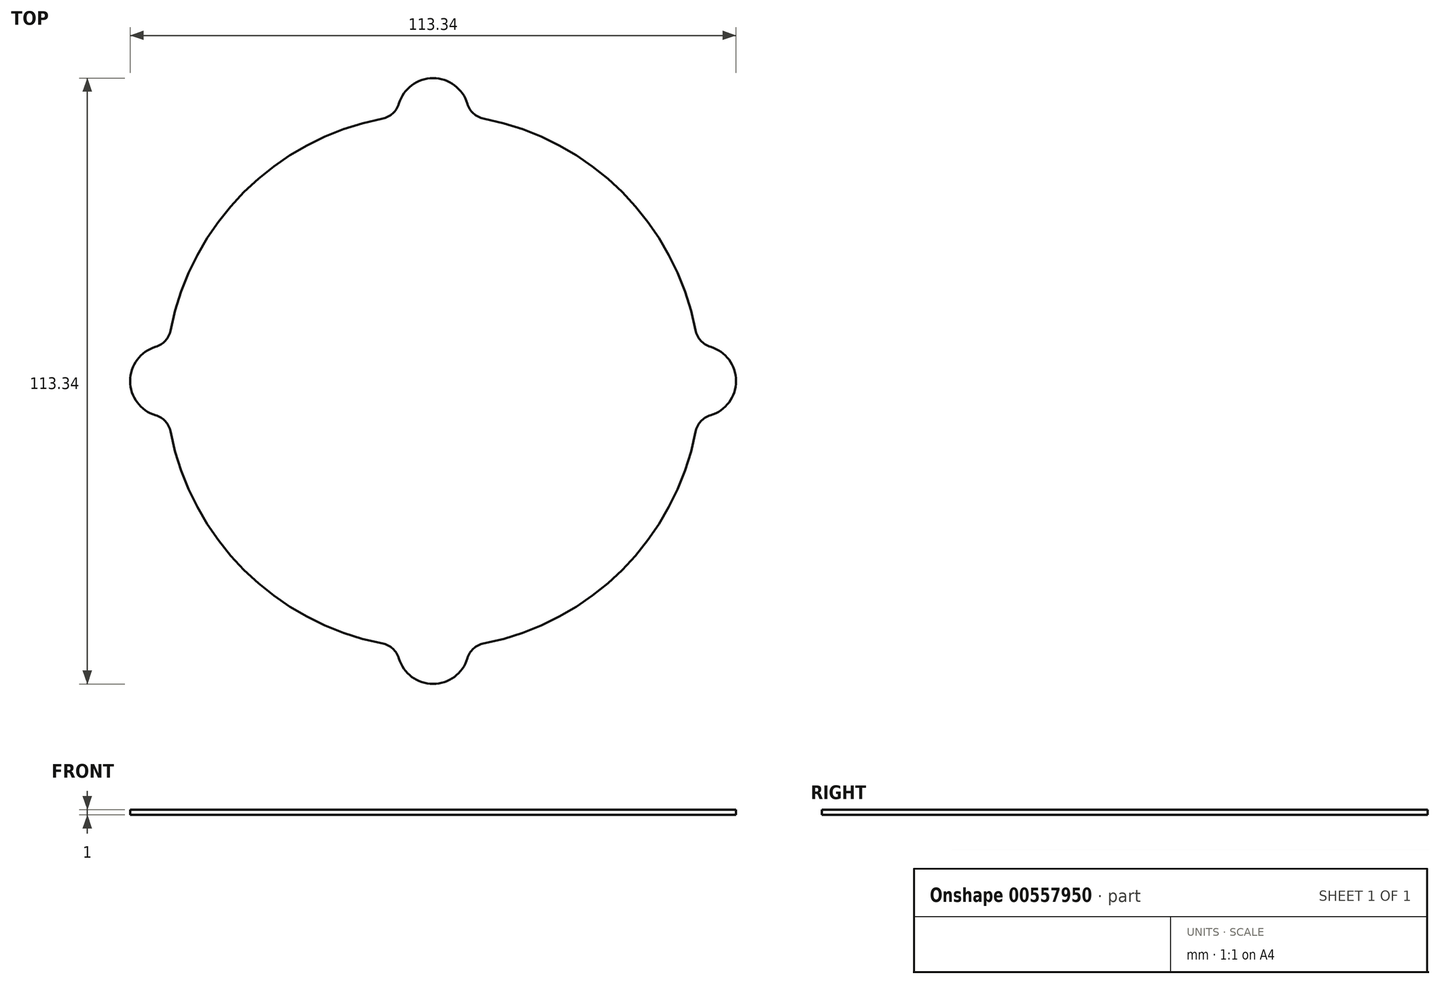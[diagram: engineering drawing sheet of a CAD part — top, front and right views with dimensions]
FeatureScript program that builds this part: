
annotation { "Feature Type Name" : "Feature", "Feature Type Description" : "" }
export const myFeature = defineFeature(function(context is Context, id is Id, definition is map)
    precondition{}
    {
        {
            assignVariable(context, id + "F0", {"name" : "t", "anyValue" : 1});
        }
        {
            var Q0;
            Q0=qCreatedBy(makeId("Top.planeOp"),FACE);
            var sketch = newSketch(context, id + "F1", { "sketchPlane" : qUnion([Q0])});
            skArc(sketch, "E0", {"start": v(-49.1, -9.47) * mm, "mid": v(-35.36, -35.36) * mm, "end": v(-9.47, -49.1) * mm});
            skCircle(sketch, "E1", {"center": v(50, 0) * mm, "radius": 6.67 * mm, "construction": true});
            skArc(sketch, "E2", {"start": v(6.65, 49.56) * mm, "mid": v(0, 56.67) * mm, "end": v(-6.65, 49.56) * mm, "construction": true});
            skArc(sketch, "E3", {"start": v(-49.56, 6.65) * mm, "mid": v(-56.67, 0) * mm, "end": v(-49.56, -6.65) * mm, "construction": true});
            skCircle(sketch, "E4", {"center": v(0, -50) * mm, "radius": 6.67 * mm, "construction": true});
            skArc(sketch, "E5.trimOffspring", {"start": v(-9.47, 49.1) * mm, "mid": v(-35.36, 35.36) * mm, "end": v(-49.1, 9.47) * mm});
            skArc(sketch, "E6", {"start": v(-6.4, -51.89) * mm, "mid": v(0, -56.67) * mm, "end": v(6.4, -51.89) * mm});
            skArc(sketch, "E7.trimOffspring", {"start": v(9.47, -49.1) * mm, "mid": v(35.36, -35.36) * mm, "end": v(49.1, -9.47) * mm});
            skPoint(sketch, "E8.visualSharp", {"position": v(6.65, -49.56) * mm});
            skArc(sketch, "E8.filletArc", {"start": v(9.47, -49.1) * mm, "mid": v(7.54, -50.06) * mm, "end": v(6.4, -51.89) * mm});
            skPoint(sketch, "E9", {"position": v(-56.67, 0) * mm});
            skPoint(sketch, "E10", {"position": v(0, 56.67) * mm});
            skPoint(sketch, "E11", {"position": v(56.67, 0) * mm});
            skArc(sketch, "E12", {"start": v(-51.89, 6.4) * mm, "mid": v(-56.67, 0) * mm, "end": v(-51.89, -6.4) * mm});
            skArc(sketch, "E13", {"start": v(6.4, 51.89) * mm, "mid": v(0, 56.67) * mm, "end": v(-6.4, 51.89) * mm});
            skArc(sketch, "E14", {"start": v(51.89, -6.4) * mm, "mid": v(56.67, 0) * mm, "end": v(51.89, 6.4) * mm});
            skArc(sketch, "E15.trimOffspring", {"start": v(49.1, 9.47) * mm, "mid": v(35.36, 35.36) * mm, "end": v(9.47, 49.1) * mm});
            skPoint(sketch, "E16.visualSharp", {"position": v(-6.65, -49.56) * mm});
            skArc(sketch, "E16.filletArc", {"start": v(-6.4, -51.89) * mm, "mid": v(-7.54, -50.06) * mm, "end": v(-9.47, -49.1) * mm});
            skPoint(sketch, "E17.visualSharp", {"position": v(-49.56, -6.65) * mm});
            skArc(sketch, "E17.filletArc", {"start": v(-49.1, -9.47) * mm, "mid": v(-50.06, -7.54) * mm, "end": v(-51.89, -6.4) * mm});
            skPoint(sketch, "E18.visualSharp", {"position": v(-49.56, 6.65) * mm});
            skArc(sketch, "E18.filletArc", {"start": v(-51.89, 6.4) * mm, "mid": v(-50.06, 7.54) * mm, "end": v(-49.1, 9.47) * mm});
            skPoint(sketch, "E19.visualSharp", {"position": v(-6.65, 49.56) * mm});
            skArc(sketch, "E19.filletArc", {"start": v(-9.47, 49.1) * mm, "mid": v(-7.54, 50.06) * mm, "end": v(-6.4, 51.89) * mm});
            skPoint(sketch, "E20.visualSharp", {"position": v(6.65, 49.56) * mm});
            skArc(sketch, "E20.filletArc", {"start": v(6.4, 51.89) * mm, "mid": v(7.54, 50.06) * mm, "end": v(9.47, 49.1) * mm});
            skPoint(sketch, "E21.visualSharp", {"position": v(49.56, 6.65) * mm});
            skArc(sketch, "E21.filletArc", {"start": v(49.1, 9.47) * mm, "mid": v(50.06, 7.54) * mm, "end": v(51.89, 6.4) * mm});
            skPoint(sketch, "E22.visualSharp", {"position": v(49.56, -6.65) * mm});
            skArc(sketch, "E22.filletArc", {"start": v(51.89, -6.4) * mm, "mid": v(50.06, -7.54) * mm, "end": v(49.1, -9.47) * mm});
            skSolve(sketch);
        }
        {
            var Q0;
            Q0=makeQuery(id+"F1.imprint","IMPRINT",FACE,{"disambiguationData":[TD([[makeQuery(id+"F1.imprint","IMPRINT",EDGE,{"derivedFrom":sQuery(id+"F1.wireOp",EDGE,"E0")}),1.0]])]});
            extrude(context, id + "F2", {"entities" : qUnion([Q0]), "depth" : (getVariable(context, 't')) * mm, "offsetDistance" : 25 * mm});
        }
    });
